# Revit family: Building-ConnessioniIEC309-GEWISS-67IB-PRESE-INTERBLOCCATE_IP67_CON_FONDO_MOD
name_source: partatom
category: Apparecchi elettrici
units: mm (PartAtom-declared; Revit-internal decimal feet)

## family parameters
Condiviso = Sì
Host = Superficie
Mantenere orientamento annotazione = Sì
Punto di calcolo locali = Sì
Quota connettore circolare = Usa diametro
Taglio con vuoti quando caricato = Sì
Tipo di parte = Normale

## types (18) — shared parameters
Catalogo = BUILDING
Catalogo Serie = 67 IB
Codice Electrocod = 2222
Con fondo = Si
Corpo presa = Light Blue
Frequenza = 50/60 Hz
Frequenza nominale (Hz) = 50/60 Hz
Glow Wire Test = 850 °C (Presa IB) - 650 °C (Cassetta di fondo)
Glow wire test: = 850 °C (Presa IB) - 650 °C (Cassetta di fondo)
Grado di protezione = IP67
IDF = c5cc221d-f519-4b81-87c7-1bbe18b35f3f
IDT = eae14658-a5a4-4161-b788-45d16122de7f
Immagine tipo = B.jpg
Interruttore = MT 6 kA Curva C
Produttore = GEWISS S.p.A.
Prospetto di default = 1219 mm
Protezione = Magnetotermico
Resistenza agli urti = IK08
SEO = Presa
Scheda Tecnica = https://www.gewiss.com
Simbolo presa = PRESAINDSTAGNA : 3P
Struttura = Grigio RAL - 7035
Temperatura di funzionamento = -25 ÷ +40 °C
Temperatura di utilizzo = -25 +40 °C
Termopressione con biglia = 125 °C (Presa IB) - 80 °C (Cassetta di fondo)
Tipologia = Verticale
URL = https://www.gewiss.com
Versione file RFA = 21.4
presa = Grigio RAL - 7035
zero-valued in all types: giallo

## per-type parameters (varying)
| type | Codice EAN | Colore | Colore: | Corrente nominale (A) | Corrente nominale (In) | Descrizione | Modello | N. poli | Numero di poli | Riferimento h | Tensione nominale | Tensione nominale: |
| GW66070N - PR.BL.IP67 C.F.3P+N+T 32A 400V 6H MT60C | 8011564740952 | Rosso | Rosso | 32 | 32 | PR.BL.IP67 C.F.3P+N+T 32A 400V 6H MT60C | GW66070N | 3P+N+T | 3P+N+T | 6 | 380 - 415 V | 380 - 415 V |
| GW66069N - PR.BL IP67 C.F.3P+T 32A 400V 6H MT60C | 8011564740945 | Rosso | Rosso | 32 | 32 | PR.BL IP67 C.F.3P+T 32A 400V 6H MT60C | GW66069N | 3P+T | 3P+T | 6 | 380 - 415 V | 380 - 415 V |
| GW66059N - PR.BL IP67 C.F.3P+N+T 16A 400V 6H MT60C | 8011564742499 | Rosso | Rosso | 16 | 16 | PR.BL IP67 C.F.3P+N+T 16A 400V 6H MT60C | GW66059N | 3P+N+T | 3P+N+T | 6 | 380 - 415 V | 380 - 415 V |
| GW66052N - PR.BL IP67 C.F.3P+T 16A 110V 4H MT60C | 8011564740822 | Giallo | Giallo | 16 | 16 | PR.BL IP67 C.F.3P+T 16A 110V 4H MT60C | GW66052N | 3P+T | 3P+T | 4 | 100 - 130 V | 100 - 130 V |
| GW66065N - PR.BL IP67 C.F.2P+T 32A 230V 6H MT60C | 8011564742505 | Blu | Blu | 32 | 32 | PR.BL IP67 C.F.2P+T 32A 230V 6H MT60C | GW66065N | 2P+T | 2P+T | 6 | 200 - 250 V | 200 - 250 V |
| GW66067N - PR.BL IP67 C.F.3P+N+T 32A 230V 9H MT60C | 8011564740921 | Blu | Blu | 32 | 32 | PR.BL IP67 C.F.3P+N+T 32A 230V 9H MT60C | GW66067N | 3P+N+T | 3P+N+T | 9 | 200 - 250 V | 200 - 250 V |
| GW66064N - PR.BL IP67 C.F.3P+N+T 32A 110V 4H MT60C | 8011564740907 | Giallo | Giallo | 32 | 32 | PR.BL IP67 C.F.3P+N+T 32A 110V 4H MT60C | GW66064N | 3P+N+T | 3P+N+T | 4 | 100 - 130 V | 100 - 130 V |
| GW66055N - PR.BL IP67 C.F.3P+T 16A 230V 9H MT60C | 8011564740846 | Blu | Blu | 16 | 16 | PR.BL IP67 C.F.3P+T 16A 230V 9H MT60C | GW66055N | 3P+T | 3P+T | 9 | 200 - 250 V | 200 - 250 V |
| GW66062N - PR.BL IP67 C.F.2P+T 32A 110V 4H MT60C | 8011564740884 | Giallo | Giallo | 32 | 32 | PR.BL IP67 C.F.2P+T 32A 110V 4H MT60C | GW66062N | 2P+T | 2P+T | 4 | 100 - 130 V | 100 - 130 V |
| GW66056N - PR.BL IP67 C.F.3P+N+T 16A 230V 9H MT60C | 8011564740853 | Blu | Blu | 16 | 16 | PR.BL IP67 C.F.3P+N+T 16A 230V 9H MT60C | GW66056N | 3P+N+T | 3P+N+T | 9 | 200 - 250 V | 200 - 250 V |
| GW66053N - PR.BL IP67 C.F.3P+N+T 16A 110V 4H MT60C | 8011564740839 | Giallo | Giallo | 16 | 16 | PR.BL IP67 C.F.3P+N+T 16A 110V 4H MT60C | GW66053N | 3P+N+T | 3P+N+T | 4 | 100 - 130 V | 100 - 130 V |
| GW66058N - PR.BL IP67 C.F.3P+T 16A 400V 6H MT60C | 8011564740877 | Rosso | Rosso | 16 | 16 | PR.BL IP67 C.F.3P+T 16A 400V 6H MT60C | GW66058N | 3P+T | 3P+T | 6 | 380 - 415 V | 380 - 415 V |
| GW66066N - PR.BL IP67 C.F.3P+T 32A 230V 9H MT60C | 8011564740914 | Blu | Blu | 32 | 32 | PR.BL IP67 C.F.3P+T 32A 230V 9H MT60C | GW66066N | 3P+T | 3P+T | 9 | 200 - 250 V | 200 - 250 V |
| GW66063N - PR.BL IP67 C.F.3P+T 32A 110V 4H MT60C | 8011564740891 | Giallo | Giallo | 32 | 32 | PR.BL IP67 C.F.3P+T 32A 110V 4H MT60C | GW66063N | 3P+T | 3P+T | 4 | 100 - 130 V | 100 - 130 V |
| GW66057N - PR.BL IP67 C.F.2P+T 16A 400V 9H MT60C | 8011564740860 | Rosso | Rosso | 16 | 16 | PR.BL IP67 C.F.2P+T 16A 400V 9H MT60C | GW66057N | 2P+T | 2P+T | 9 | 380 - 415 V | 380 - 415 V |
| GW66054N - PR.BL IP67 C.F.2P+T 16A 230V 6H MT60C | 8011564742482 | Blu | Blu | 16 | 16 | PR.BL IP67 C.F.2P+T 16A 230V 6H MT60C | GW66054N | 2P+T | 2P+T | 6 | 200 - 250 V | 200 - 250 V |
| GW66068N - PR.BL IP67 C.F.2P+T 32A 400V 9H MT60C | 8011564740938 | Rosso | Rosso | 32 | 32 | PR.BL IP67 C.F.2P+T 32A 400V 9H MT60C | GW66068N | 2P+T | 2P+T | 9 | 380 - 415 V | 380 - 415 V |
| GW66051N - PR.BL IP67 C.F.2P+T 16A 110V 4H MT60C | 8011564740815 | Giallo | Giallo | 16 | 16 | PR.BL IP67 C.F.2P+T 16A 110V 4H MT60C | GW66051N | 2P+T | 2P+T | 4 | 100 - 130 V | 100 - 130 V |

## geometry (parser evidence)
native form markers: Sweep x3
no freeform markers — native parametric forms only
